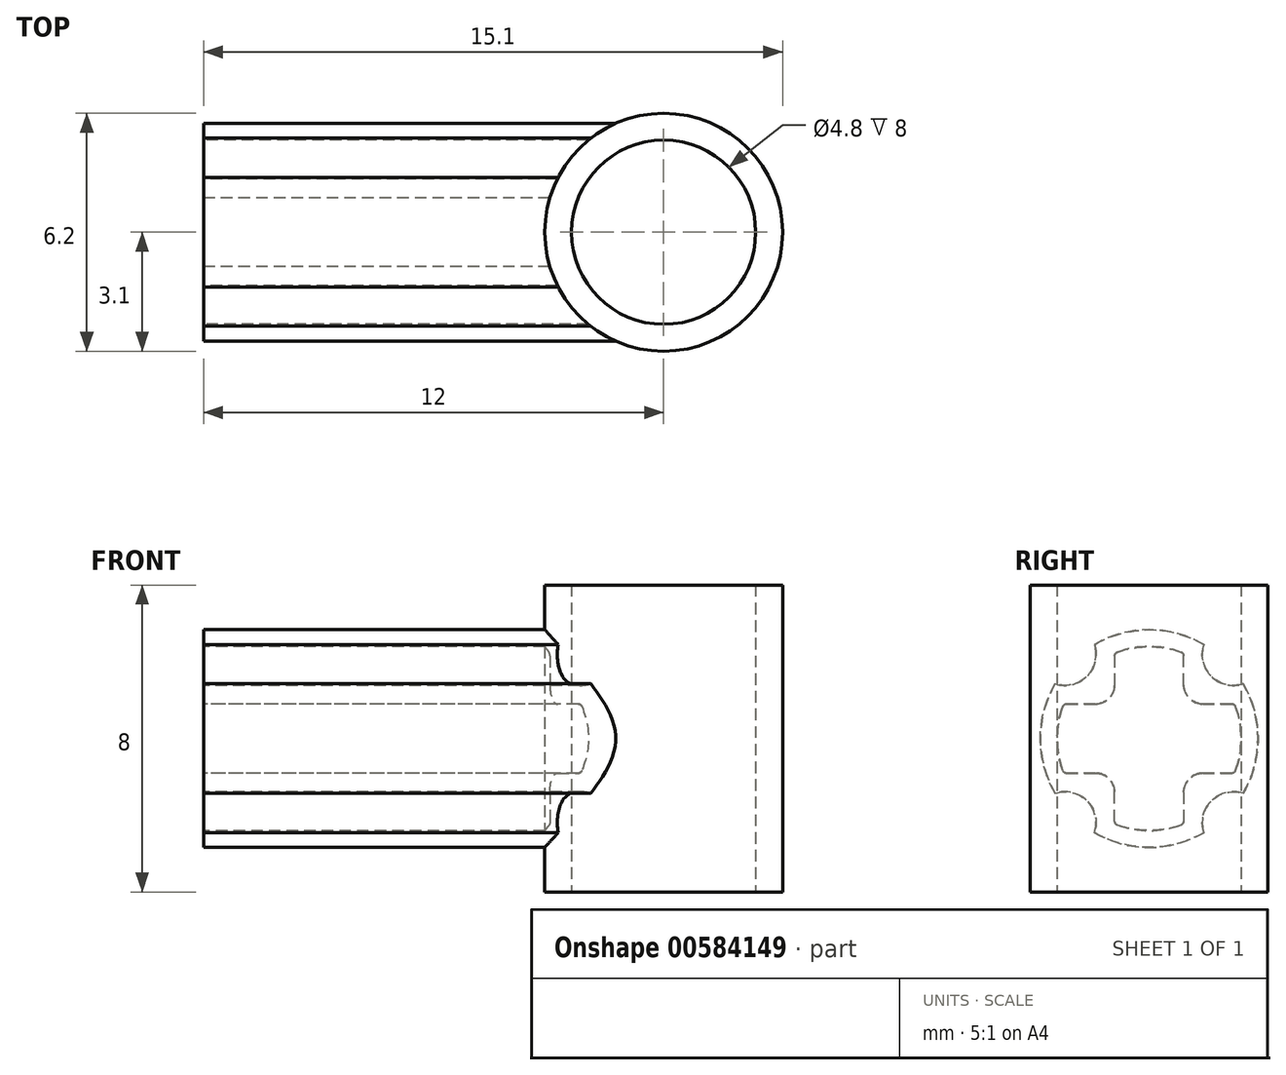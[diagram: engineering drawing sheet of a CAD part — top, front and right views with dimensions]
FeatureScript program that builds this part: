
annotation { "Feature Type Name" : "Feature", "Feature Type Description" : "" }
export const myFeature = defineFeature(function(context is Context, id is Id, definition is map)
    precondition{}
    {
        {
            var Q0;
            Q0=qCreatedBy(makeId("Top.planeOp"),FACE);
            var sketch = newSketch(context, id + "F0", { "sketchPlane" : qUnion([Q0])});
            skArc(sketch, "E0", {"start": v(0, 2.4) * mm, "mid": v(-2.4, 0) * mm, "end": v(0, -2.4) * mm});
            skArc(sketch, "E1", {"start": v(0, 3.1) * mm, "mid": v(-3.1, 0) * mm, "end": v(0, -3.1) * mm});
            skLineSegment(sketch, "E2", {"start": v(0, 3.1) * mm, "end": v(0, 2.4) * mm});
            skLineSegment(sketch, "E3", {"start": v(0, -2.4) * mm, "end": v(0, -3.1) * mm});
            skSolve(sketch);
        }
        {
            var Q0;
            Q0=qSketchRegion(id+"F0",true);
            extrude(context, id + "F1", {"entities" : qUnion([Q0]), "depth" : 4 * mm, "offsetDistance" : 25 * mm});
        }
        {
            var Q0;
            Q0=makeQuery(id+"F1.opExtrude","CAP_VERTEX",VERTEX,{"disambiguationData":[OSD([sQuery(id+"F0.wireOp",EDGE,"E1"),sQuery(id+"F0.wireOp",EDGE,"E2")])],"isStart":false});
            var Q1;
            Q1=makeQuery(id+"F1.opExtrude","CAP_VERTEX",VERTEX,{"disambiguationData":[OSD([sQuery(id+"F0.wireOp",EDGE,"E0"),sQuery(id+"F0.wireOp",EDGE,"E2")])],"isStart":false});
            var Q2;
            Q2=makeQuery(id+"F1.opExtrude","CAP_VERTEX",VERTEX,{"disambiguationData":[OSD([sQuery(id+"F0.wireOp",EDGE,"E0"),sQuery(id+"F0.wireOp",EDGE,"E2")])],"isStart":true});
            cPlane(context, id + "F2", {"entities" : qUnion([Q0, Q1, Q2]), "cplaneType" : CPlaneType.THREE_POINT, "offset" : 25 * mm, "width" : 150 * mm, "height" : 150 * mm});
        }
        {
            var Q0;
            Q0=qCreatedBy(id+"F2.planeOp",FACE);
            cPlane(context, id + "F3", {"entities" : qUnion([Q0]), "cplaneType" : CPlaneType.OFFSET, "offset" : 12 * mm, "width" : 150 * mm, "height" : 150 * mm});
        }
        {
            var Q0;
            Q0=qCreatedBy(id+"F3.planeOp",FACE);
            var sketch = newSketch(context, id + "F4", { "sketchPlane" : qUnion([Q0])});
            skLineSegment(sketch, "E4.0", {"start": v(2.4, 0) * mm, "end": v(3.1, 0) * mm, "construction": true});
            skLineSegment(sketch, "E4.1", {"start": v(-3.1, 0) * mm, "end": v(-2.4, 0) * mm, "construction": true});
            skLineSegment(sketch, "E5", {"start": v(-2.4, 0) * mm, "end": v(2.4, 0) * mm, "construction": true});
            skLineSegment(sketch, "E6", {"start": v(0, 1.65) * mm, "end": v(0, -0.27) * mm, "construction": true});
            skPoint(sketch, "E6.startSnap0", {"position": v(0, 0) * mm});
            skLineSegment(sketch, "E7", {"start": v(0, 5.29) * mm, "end": v(0, 1.3) * mm, "construction": true});
            skLineSegment(sketch, "E8.0", {"start": v(-0.9, 1.4) * mm, "end": v(-0.9, 2.16) * mm});
            skArc(sketch, "E8.1", {"start": v(-0.9, 2.16) * mm, "mid": v(-0.88, 2.21) * mm, "end": v(-0.83, 2.25) * mm});
            skArc(sketch, "E8.2", {"start": v(-0.83, 2.25) * mm, "mid": v(0, 2.4) * mm, "end": v(0.83, 2.25) * mm});
            skArc(sketch, "E8.3", {"start": v(0.83, 2.25) * mm, "mid": v(0.88, 2.21) * mm, "end": v(0.9, 2.16) * mm});
            skLineSegment(sketch, "E8.4", {"start": v(0.9, 2.16) * mm, "end": v(0.9, 1.4) * mm});
            skArc(sketch, "E8.5", {"start": v(0.9, 1.4) * mm, "mid": v(1.05, 1.05) * mm, "end": v(1.4, 0.9) * mm});
            skLineSegment(sketch, "E8.6", {"start": v(1.4, 0.9) * mm, "end": v(2.16, 0.9) * mm});
            skArc(sketch, "E8.7", {"start": v(-1.4, 0.9) * mm, "mid": v(-1.05, 1.05) * mm, "end": v(-0.9, 1.4) * mm});
            skLineSegment(sketch, "E8.8", {"start": v(-2.16, 0.9) * mm, "end": v(-1.4, 0.9) * mm});
            skArc(sketch, "E8.10", {"start": v(-2.25, 0.83) * mm, "mid": v(-2.21, 0.88) * mm, "end": v(-2.16, 0.9) * mm});
            skArc(sketch, "E8.11", {"start": v(2.16, 0.9) * mm, "mid": v(2.21, 0.88) * mm, "end": v(2.25, 0.83) * mm});
            skArc(sketch, "E8.12", {"start": v(2.25, 0.83) * mm, "mid": v(2.36, 0.42) * mm, "end": v(2.4, 0) * mm});
            skArc(sketch, "E9", {"start": v(-2.4, 0) * mm, "mid": v(-2.36, 0.42) * mm, "end": v(-2.25, 0.83) * mm});
            skArc(sketch, "E10.MirrorCS", {"start": v(-2.25, -0.83) * mm, "mid": v(-2.21, -0.88) * mm, "end": v(-2.16, -0.9) * mm});
            skArc(sketch, "E11.MirrorCS", {"start": v(2.16, -0.9) * mm, "mid": v(2.21, -0.88) * mm, "end": v(2.25, -0.83) * mm});
            skArc(sketch, "E12.MirrorCS", {"start": v(0.83, -2.25) * mm, "mid": v(0.88, -2.21) * mm, "end": v(0.9, -2.16) * mm});
            skArc(sketch, "E13.MirrorCS", {"start": v(-0.9, -2.16) * mm, "mid": v(-0.88, -2.21) * mm, "end": v(-0.83, -2.25) * mm});
            skLineSegment(sketch, "E14.MirrorCS", {"start": v(-2.16, -0.9) * mm, "end": v(-1.4, -0.9) * mm});
            skArc(sketch, "E15.MirrorCS", {"start": v(2.25, -0.83) * mm, "mid": v(2.36, -0.42) * mm, "end": v(2.4, 0) * mm});
            skArc(sketch, "E16.MirrorCS", {"start": v(-2.4, 0) * mm, "mid": v(-2.36, -0.42) * mm, "end": v(-2.25, -0.83) * mm});
            skLineSegment(sketch, "E17.MirrorCS", {"start": v(0, -1.65) * mm, "end": v(0, 0.27) * mm, "construction": true});
            skLineSegment(sketch, "E18.MirrorCS", {"start": v(0.9, -2.16) * mm, "end": v(0.9, -1.4) * mm});
            skLineSegment(sketch, "E19.MirrorCS", {"start": v(-0.9, -1.4) * mm, "end": v(-0.9, -2.16) * mm});
            skLineSegment(sketch, "E20.MirrorCS", {"start": v(0, -5.29) * mm, "end": v(0, -1.3) * mm, "construction": true});
            skArc(sketch, "E21.MirrorCS", {"start": v(-1.4, -0.9) * mm, "mid": v(-1.05, -1.05) * mm, "end": v(-0.9, -1.4) * mm});
            skArc(sketch, "E22.MirrorCS", {"start": v(0.9, -1.4) * mm, "mid": v(1.05, -1.05) * mm, "end": v(1.4, -0.9) * mm});
            skArc(sketch, "E23.MirrorCS", {"start": v(-0.83, -2.25) * mm, "mid": v(0, -2.4) * mm, "end": v(0.83, -2.25) * mm});
            skLineSegment(sketch, "E24.MirrorCS", {"start": v(1.4, -0.9) * mm, "end": v(2.16, -0.9) * mm});
            skArc(sketch, "E25", {"start": v(-2.84, 0) * mm, "mid": v(-2.74, 0.74) * mm, "end": v(-2.45, 1.43) * mm});
            skLineSegment(sketch, "E26", {"start": v(0, 0) * mm, "end": v(-2.67, 2.67) * mm, "construction": true});
            skArc(sketch, "E27", {"start": v(-2.45, 1.43) * mm, "mid": v(-2, 1.4) * mm, "end": v(-1.62, 1.62) * mm});
            skArc(sketch, "E28.MirrorCS", {"start": v(-1.43, 2.45) * mm, "mid": v(-1.4, 2) * mm, "end": v(-1.62, 1.62) * mm});
            skArc(sketch, "E29.MirrorCS", {"start": v(0, 2.84) * mm, "mid": v(-0.74, 2.74) * mm, "end": v(-1.43, 2.45) * mm});
            skArc(sketch, "E30.MirrorCS", {"start": v(0, 2.84) * mm, "mid": v(0.74, 2.74) * mm, "end": v(1.43, 2.45) * mm});
            skArc(sketch, "E31.MirrorCS", {"start": v(2.45, 1.43) * mm, "mid": v(2, 1.4) * mm, "end": v(1.62, 1.62) * mm});
            skArc(sketch, "E32.MirrorCS", {"start": v(1.43, 2.45) * mm, "mid": v(1.4, 2) * mm, "end": v(1.62, 1.62) * mm});
            skArc(sketch, "E33.MirrorCS", {"start": v(2.84, 0) * mm, "mid": v(2.74, 0.74) * mm, "end": v(2.45, 1.43) * mm});
            skArc(sketch, "E34.MirrorCS", {"start": v(-2.84, 0) * mm, "mid": v(-2.74, -0.74) * mm, "end": v(-2.45, -1.43) * mm});
            skArc(sketch, "E35.MirrorCS", {"start": v(-2.45, -1.43) * mm, "mid": v(-2, -1.4) * mm, "end": v(-1.62, -1.62) * mm});
            skArc(sketch, "E36.MirrorCS", {"start": v(-1.43, -2.45) * mm, "mid": v(-1.4, -2) * mm, "end": v(-1.62, -1.62) * mm});
            skArc(sketch, "E37.MirrorCS", {"start": v(0, -2.84) * mm, "mid": v(-0.74, -2.74) * mm, "end": v(-1.43, -2.45) * mm});
            skArc(sketch, "E38.MirrorCS", {"start": v(0, -2.84) * mm, "mid": v(0.74, -2.74) * mm, "end": v(1.43, -2.45) * mm});
            skArc(sketch, "E39.MirrorCS", {"start": v(1.43, -2.45) * mm, "mid": v(1.4, -2) * mm, "end": v(1.62, -1.62) * mm});
            skArc(sketch, "E40.MirrorCS", {"start": v(2.45, -1.43) * mm, "mid": v(2, -1.4) * mm, "end": v(1.62, -1.62) * mm});
            skArc(sketch, "E41.MirrorCS", {"start": v(2.84, 0) * mm, "mid": v(2.74, -0.74) * mm, "end": v(2.45, -1.43) * mm});
            skSolve(sketch);
        }
        {
            var Q0;
            Q0=makeQuery(id+"F1.opExtrude","SWEPT_BODY",BODY,{"disambiguationData":[OSD([sQuery(id+"F0.wireOp",EDGE,"E0"),sQuery(id+"F0.wireOp",EDGE,"E1"),sQuery(id+"F0.wireOp",EDGE,"E2"),sQuery(id+"F0.wireOp",EDGE,"E3")])]});
            var Q1;
            Q1=makeQuery(id+"F1.opExtrude","SWEPT_FACE",FACE,{"disambiguationData":[OSD([sQuery(id+"F0.wireOp",EDGE,"E2")])]});
            mirror(context, id + "F5", {"operationType" : NewBodyOperationType.ADD, "entities" : qUnion([Q0]), "mirrorPlane" : qUnion([Q1])});
        }
        {
            var Q0;
            Q0=makeQuery(id+"F1.opExtrude","SWEPT_BODY",BODY,{"disambiguationData":[OSD([sQuery(id+"F0.wireOp",EDGE,"E0"),sQuery(id+"F0.wireOp",EDGE,"E1"),sQuery(id+"F0.wireOp",EDGE,"E2"),sQuery(id+"F0.wireOp",EDGE,"E3")])]});
            var Q1;
            {var subQ0=makeQuery(id+"F1.opExtrude","CAP_FACE",FACE,{"disambiguationData":[OSD([sQuery(id+"F0.wireOp",EDGE,"E0"),sQuery(id+"F0.wireOp",EDGE,"E1"),sQuery(id+"F0.wireOp",EDGE,"E2"),sQuery(id+"F0.wireOp",EDGE,"E3")])],"isStart":true});Q1=makeQuery(id+"F5.boolean.opBoolean","MERGE",FACE,{"derivedFrom":[subQ0,makeQuery(id+"F5.opPattern","COPY",FACE,{"derivedFrom":subQ0,"instanceName":"1"})]});}
            mirror(context, id + "F6", {"operationType" : NewBodyOperationType.ADD, "entities" : qUnion([Q0]), "mirrorPlane" : qUnion([Q1])});
        }
        {
            var Q0;
            Q0=makeQuery(id+"F4.imprint","IMPRINT",FACE,{"disambiguationData":[TD([[makeQuery(id+"F4.imprint","IMPRINT",EDGE,{"derivedFrom":sQuery(id+"F4.wireOp",EDGE,"E8.0")}),1.0]])]});
            var Q1;
            Q1=makeQuery(id+"F1.opExtrude","SWEPT_BODY",BODY,{"disambiguationData":[OSD([sQuery(id+"F0.wireOp",EDGE,"E0"),sQuery(id+"F0.wireOp",EDGE,"E1"),sQuery(id+"F0.wireOp",EDGE,"E2"),sQuery(id+"F0.wireOp",EDGE,"E3")])]});
            extrude(context, id + "F7", {"entities" : qUnion([Q0]), "operationType" : NewBodyOperationType.ADD, "endBound" : BoundingType.UP_TO_BODY, "oppositeDirection" : true, "depth" : 25 * mm, "endBoundEntityBody" : qUnion([Q1]), "offsetDistance" : 25 * mm});
        }
        {
            var Q0;
            Q0=qCreatedBy(id+"F2.planeOp",FACE);
            var sketch = newSketch(context, id + "F8", { "sketchPlane" : qUnion([Q0])});
            skLineSegment(sketch, "E42.0", {"start": v(-2.4, 4) * mm, "end": v(2.4, 4) * mm, "construction": true});
            skLineSegment(sketch, "E43", {"start": v(0, 6.73) * mm, "end": v(0, -1.8) * mm, "construction": true});
            skPoint(sketch, "E43.startSnap0", {"position": v(0, 4) * mm});
            skSolve(sketch);
        }
    });
